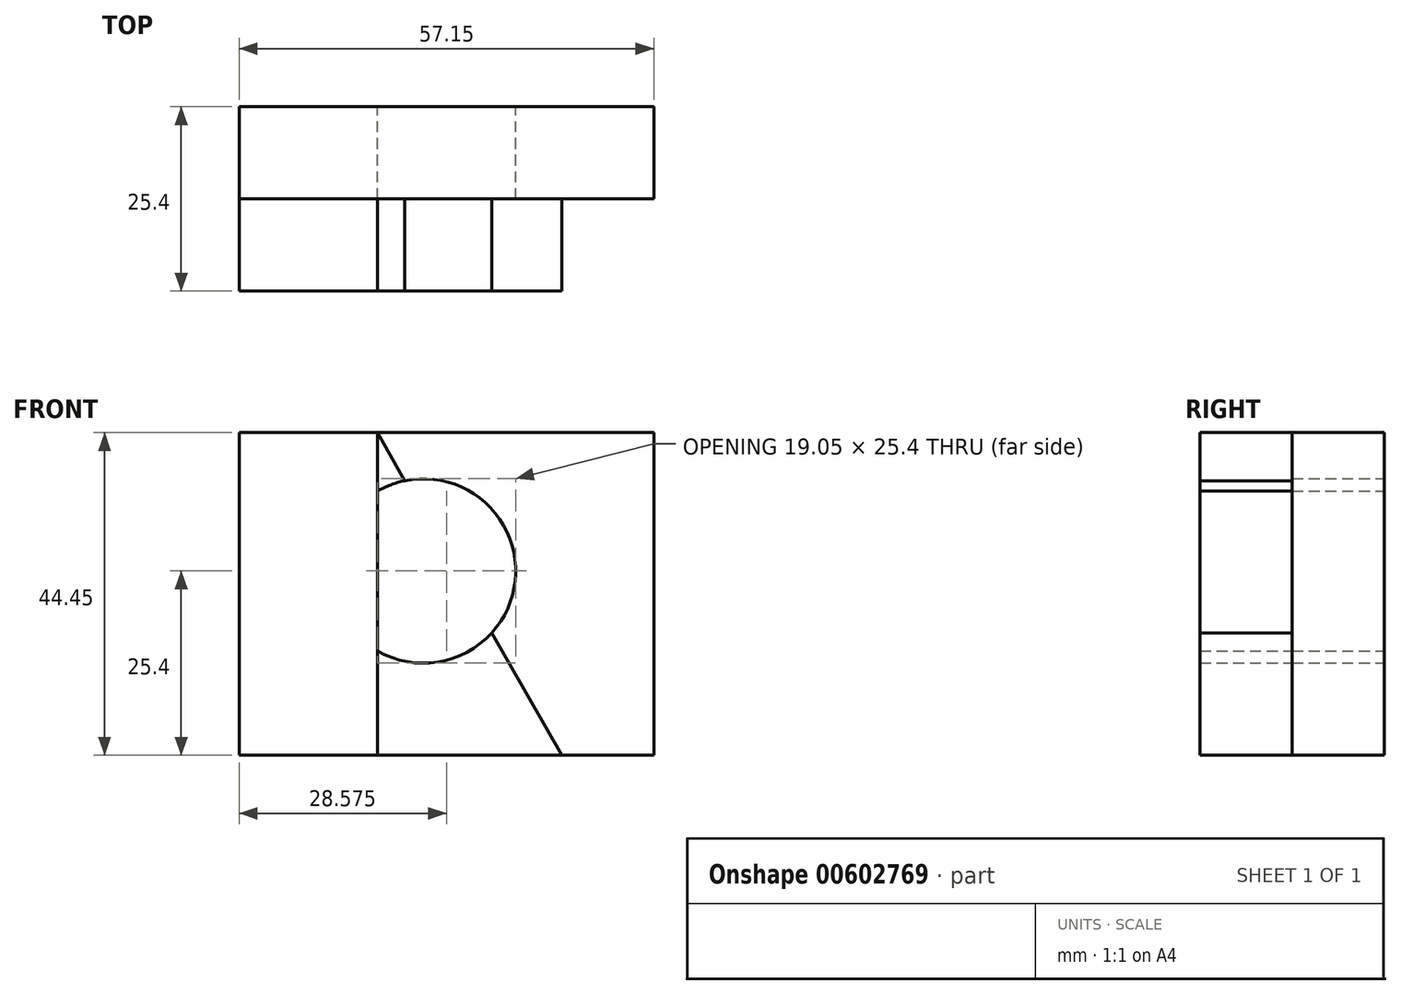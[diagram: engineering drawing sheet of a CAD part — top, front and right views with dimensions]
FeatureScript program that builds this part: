
annotation { "Feature Type Name" : "Feature", "Feature Type Description" : "" }
export const myFeature = defineFeature(function(context is Context, id is Id, definition is map)
    precondition{}
    {
        {
            var Q0;
            Q0=qCreatedBy(makeId("Front.planeOp"),FACE);
            var sketch = newSketch(context, id + "F0", { "sketchPlane" : qUnion([Q0])});
            skLineSegment(sketch, "E0", {"start": v(0, 0) * mm, "end": v(57.15, 0) * mm});
            skLineSegment(sketch, "E1", {"start": v(57.15, 0) * mm, "end": v(57.15, 44.45) * mm});
            skLineSegment(sketch, "E2", {"start": v(57.15, 44.45) * mm, "end": v(0, 44.45) * mm});
            skLineSegment(sketch, "E3", {"start": v(0, 44.45) * mm, "end": v(0, 0) * mm});
            skSolve(sketch);
        }
        {
            var Q0;
            Q0 = qSketchRegion(id + "F0", true);
            extrude(context, id + "F1", {"entities" : qUnion([Q0]), "depth" : 12.7 * mm, "offsetDistance" : 25.4 * mm});
        }
        {
            var Q0;
            Q0=makeQuery(id+"F1.opExtrude","SWEPT_FACE",FACE,{"disambiguationData":[OSD([sQuery(id+"F0.wireOp",EDGE,"E2")])]});
            var sketch = newSketch(context, id + "F2", { "sketchPlane" : qUnion([Q0])});
            skLineSegment(sketch, "E4", {"start": v(0, -12.7) * mm, "end": v(0, -25.4) * mm});
            skLineSegment(sketch, "E5", {"start": v(0, -25.4) * mm, "end": v(19.05, -25.4) * mm});
            skLineSegment(sketch, "E6", {"start": v(19.05, -25.4) * mm, "end": v(19.05, -12.7) * mm});
            skSolve(sketch);
        }
        {
            var Q0;
            {var subQ0=sQuery(id+"F2.wireOp",EDGE,"E4");Q0=makeQuery(id+"F2.imprint","IMPRINT",FACE,{"disambiguationData":[TD([[makeQuery(id+"F2.imprint","IMPRINT",EDGE,{"derivedFrom":subQ0}),1.0]])]});}
            extrude(context, id + "F3", {"entities" : qUnion([Q0]), "oppositeDirection" : true, "depth" : 44.45 * mm, "offsetDistance" : 25.4 * mm});
        }
        {
            var Q0;
            Q0=makeQuery(id+"F1.opExtrude","CAP_FACE",FACE,{"disambiguationData":[OSD([sQuery(id+"F0.wireOp",EDGE,"E0"),sQuery(id+"F0.wireOp",EDGE,"E1"),sQuery(id+"F0.wireOp",EDGE,"E2"),sQuery(id+"F0.wireOp",EDGE,"E3")])],"isStart":false});
            var sketch = newSketch(context, id + "F4", { "sketchPlane" : qUnion([Q0])});
            skLineSegment(sketch, "E7.0.0", {"start": v(57.15, 44.45) * mm, "end": v(0, 44.45) * mm});
            skLineSegment(sketch, "E7.0.1", {"start": v(0, 44.45) * mm, "end": v(0, 0) * mm});
            skLineSegment(sketch, "E7.0.2", {"start": v(0, 0) * mm, "end": v(57.15, 0) * mm});
            skLineSegment(sketch, "E7.0.3", {"start": v(57.15, 0) * mm, "end": v(57.15, 44.45) * mm});
            skPoint(sketch, "E8.0", {"position": v(19.05, 44.45) * mm});
            skLineSegment(sketch, "E9.0.2", {"start": v(0, 44.45) * mm, "end": v(57.15, 44.45) * mm});
            skLineSegment(sketch, "E10", {"start": v(19.05, 44.45) * mm, "end": v(44.45, 0) * mm});
            skLineSegment(sketch, "E11", {"start": v(19.05, 44.45) * mm, "end": v(19.05, 0) * mm});
            skLineSegment(sketch, "E12", {"start": v(19.05, 0) * mm, "end": v(44.45, 0) * mm});
            skSolve(sketch);
        }
        {
            var Q0;
            Q0=makeQuery(id+"F4.imprint","IMPRINT",FACE,{"disambiguationData":[TD([[makeQuery(id+"F4.imprint","IMPRINT",EDGE,{"derivedFrom":sQuery(id+"F4.wireOp",EDGE,"E10")}),-1.0]])]});
            extrude(context, id + "F5", {"entities" : qUnion([Q0]), "depth" : 12.7 * mm, "offsetDistance" : 25.4 * mm});
        }
        {
            var Q0;
            Q0=makeQuery(id+"F1.opExtrude","CAP_FACE",FACE,{"disambiguationData":[OSD([sQuery(id+"F0.wireOp",EDGE,"E0"),sQuery(id+"F0.wireOp",EDGE,"E1"),sQuery(id+"F0.wireOp",EDGE,"E2"),sQuery(id+"F0.wireOp",EDGE,"E3")])],"isStart":true});
            var sketch = newSketch(context, id + "F6", { "sketchPlane" : qUnion([Q0])});
            skLineSegment(sketch, "E13.0.0", {"start": v(-44.45, 0) * mm, "end": v(-19.05, 44.45) * mm});
            skLineSegment(sketch, "E13.0.1", {"start": v(-19.05, 44.45) * mm, "end": v(-19.05, 0) * mm});
            skLineSegment(sketch, "E13.0.2", {"start": v(-19.05, 0) * mm, "end": v(-44.45, 0) * mm});
            skLineSegment(sketch, "E14.0.0", {"start": v(-19.05, 44.45) * mm, "end": v(0, 44.45) * mm});
            skLineSegment(sketch, "E14.0.1", {"start": v(0, 44.45) * mm, "end": v(0, 0) * mm});
            skLineSegment(sketch, "E14.0.2", {"start": v(0, 0) * mm, "end": v(-19.05, 0) * mm});
            skLineSegment(sketch, "E14.0.3", {"start": v(-19.05, 0) * mm, "end": v(-19.05, 44.45) * mm});
            skLineSegment(sketch, "E15.0.0", {"start": v(-57.15, 44.45) * mm, "end": v(0, 44.45) * mm});
            skLineSegment(sketch, "E15.0.2", {"start": v(0, 0) * mm, "end": v(-57.15, 0) * mm});
            skLineSegment(sketch, "E15.0.3", {"start": v(-57.15, 0) * mm, "end": v(-57.15, 44.45) * mm});
            skPoint(sketch, "E16.centerSnap0", {"position": v(-19.05, 22.22) * mm});
            skCircle(sketch, "E17", {"center": v(-25.4, 25.4) * mm, "radius": 12.7 * mm});
            skSolve(sketch);
        }
        {
            var Q0;
            {var subQ0=sQuery(id+"F6.wireOp",EDGE,"E17");var subQ1=sQuery(id+"F6.wireOp",EDGE,"E13.0.0");var subQ2=makeQuery(id+"F6.imprint","INTERSECT",VERTEX,{"disambiguationData":[OD(0.0)],"derivedFrom":[subQ1,subQ0]});Q0=makeQuery(id+"F6.imprint","IMPRINT",FACE,{"disambiguationData":[TD([[makeQuery(id+"F6.imprint","IMPRINT",EDGE,{"disambiguationData":[TD([[subQ2,-1.0]])],"derivedFrom":subQ1}),-1.0]])]});}
            var Q1;
            {var subQ0=sQuery(id+"F6.wireOp",EDGE,"E17");var subQ1=sQuery(id+"F6.wireOp",EDGE,"E14.0.3");var subQ2=makeQuery(id+"F6.imprint","INTERSECT",VERTEX,{"disambiguationData":[OD(0.0)],"derivedFrom":[subQ1,subQ0]});Q1=makeQuery(id+"F6.imprint","IMPRINT",FACE,{"disambiguationData":[TD([[makeQuery(id+"F6.imprint","IMPRINT",EDGE,{"disambiguationData":[TD([[subQ2,-1.0]])],"derivedFrom":subQ1}),-1.0]])]});}
            extrude(context, id + "F7", {"entities" : qUnion([Q0, Q1]), "operationType" : NewBodyOperationType.REMOVE, "oppositeDirection" : true, "depth" : 25.4 * mm, "offsetDistance" : 25.4 * mm});
        }
        {
            var Q0;
            {var subQ0=sQuery(id+"F6.wireOp",EDGE,"E17");var subQ1=sQuery(id+"F6.wireOp",EDGE,"E13.0.0");var subQ2=makeQuery(id+"F6.imprint","INTERSECT",VERTEX,{"disambiguationData":[OD(0.0)],"derivedFrom":[subQ1,subQ0]});Q0=makeQuery(id+"F6.imprint","IMPRINT",FACE,{"disambiguationData":[TD([[makeQuery(id+"F6.imprint","IMPRINT",EDGE,{"disambiguationData":[TD([[subQ2,-1.0]])],"derivedFrom":subQ1}),1.0]])]});}
            extrude(context, id + "F8", {"entities" : qUnion([Q0]), "operationType" : NewBodyOperationType.REMOVE, "oppositeDirection" : true, "depth" : 25.4 * mm, "offsetDistance" : 25.4 * mm});
        }
    });
